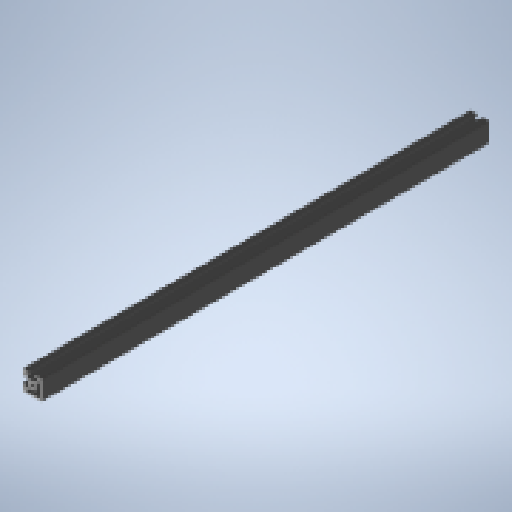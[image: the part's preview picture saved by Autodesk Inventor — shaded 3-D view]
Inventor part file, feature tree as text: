
AUTODESK INVENTOR PART (.ipt)
format: ipt  version: 2024 (Build 280153000, 153)  size: 267,264 bytes
history: native  units: mm
features: other x7, thread x2, sketch x2, extrude x1, hole x1
ambient origin geometry x8: Origin, YZ Plane, XZ Plane, XY Plane, X Axis, Y Axis, Z Axis, Center Point
bodies: Solid1 (feature_tree)
feature tree (13):
  extrude  "Extrusion1"  TaperAngle=0.0deg  [1 undecoded]
  hole  "Hole1"  [1 undecoded]
  other  "C1_XY"
  other  "C1_YZ"
  other  "C1_ZX"
  other  "C1_X"
  other  "C1_Y"
  other  "C1_Z"
  other  "C1_Center"
  thread  "Thread1"  [1 undecoded]
  thread  "Thread2"  [1 undecoded]
  sketch  "Sketch_64"  dims[d2=4.2mm d3=6.0mm d4=4.0mm d5=2.0mm d6=90.0deg d7=456.0mm d8=0.0mm d9=0.0mm d10=10.0mm d11=0.0mm d12=10.0mm d13=0.0mm]
  sketch  "Sketch2"  dims[d0=456.0mm d1=0.0mm]
note: 4 required parameter values undecoded (feature->parameter linkage not recoverable at this tier; creation-order binding heuristic only, values carry confidence <= 0.55)
